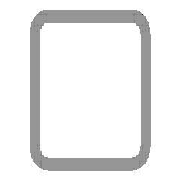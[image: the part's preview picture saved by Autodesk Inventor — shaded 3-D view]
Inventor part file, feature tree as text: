
AUTODESK INVENTOR PART (.ipt)
format: ipt  version: 2025 (Build 290162010, 162A)  size: 135,168 bytes
history: native  units: mm (DEFAULTED — no unit token found)
features: other x4, sketch x1, plane x1
ambient origin geometry x8: Origin, YZ Plane, XZ Plane, XY Plane, X Axis, Y Axis, Z Axis, Center Point
bodies: Solid1 (feature_tree), Body (feature_tree)
feature tree (6):
  parser-record x1  (decoder bookkeeping rows leaked as tree rows — omitted from the tree; the rows remain in map.json)
  other  "Driven Length"
  other  "Start Plane"
  other  "End Plane"
  sketch  "Sketch3"  dims[d3=2800.0mm d4=0.0mm d7=6.0mm d9=100.0mm d11=100.0mm d12=3.0mm d13=-0.0mm d14=2800.0mm d15=50.0mm d16=50.0mm d17=90.0deg d18=2800.0mm]
  plane  "Work Plane3"
